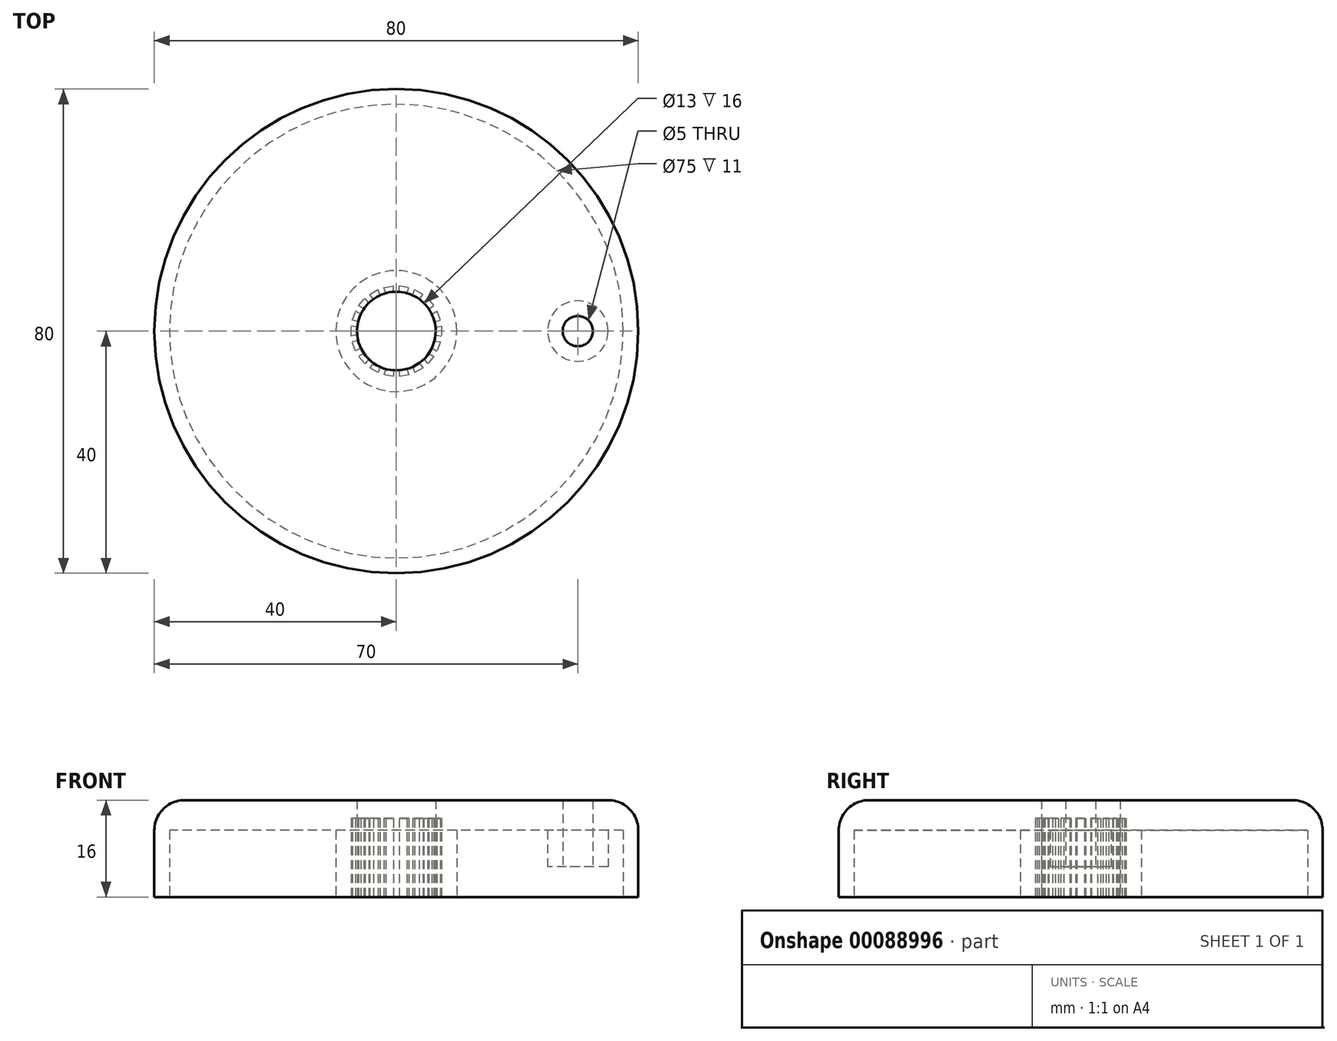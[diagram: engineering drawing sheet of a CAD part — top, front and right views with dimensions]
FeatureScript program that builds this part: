
annotation { "Feature Type Name" : "Feature", "Feature Type Description" : "" }
export const myFeature = defineFeature(function(context is Context, id is Id, definition is map)
    precondition{}
    {
        {
            var Q0;
            Q0=qCreatedBy(makeId("Top.planeOp"),FACE);
            var sketch = newSketch(context, id + "F0", { "sketchPlane" : qUnion([Q0])});
            skCircle(sketch, "E0", {"center": v(0, 0) * mm, "radius": 7.5 * mm, "construction": true});
            skLineSegment(sketch, "E1", {"start": v(0, 0) * mm, "end": v(0, 7.5) * mm, "construction": true});
            skLineSegment(sketch, "E2", {"start": v(0.5, 6.48) * mm, "end": v(0.5, 7.48) * mm});
            skLineSegment(sketch, "E3.MirrorCS", {"start": v(-0.5, 6.48) * mm, "end": v(-0.5, 7.48) * mm});
            skCircle(sketch, "E4.0", {"center": v(0, 0) * mm, "radius": 6.5 * mm, "construction": true});
            skLineSegment(sketch, "E5", {"start": v(-0.5, 6.48) * mm, "end": v(0.5, 6.48) * mm});
            skPoint(sketch, "E6.orphan", {"position": v(-0.5, 5.89) * mm});
            skPoint(sketch, "E7.orphan", {"position": v(0.5, 5.89) * mm});
            skPoint(sketch, "E8.orphan", {"position": v(0.5, 8.94) * mm});
            skPoint(sketch, "E9.orphan", {"position": v(-0.5, 8.94) * mm});
            skLineSegment(sketch, "E10.1.0", {"start": v(1.75, 6.26) * mm, "end": v(2.09, 7.2) * mm});
            skLineSegment(sketch, "E10.1.1", {"start": v(1.75, 6.26) * mm, "end": v(2.69, 5.92) * mm});
            skLineSegment(sketch, "E10.1.2", {"start": v(2.69, 5.92) * mm, "end": v(3.03, 6.86) * mm});
            skLineSegment(sketch, "E10.2.0", {"start": v(3.78, 5.29) * mm, "end": v(4.43, 6.05) * mm});
            skLineSegment(sketch, "E10.2.1", {"start": v(3.78, 5.29) * mm, "end": v(4.55, 4.64) * mm});
            skLineSegment(sketch, "E10.2.2", {"start": v(4.55, 4.64) * mm, "end": v(5.2, 5.41) * mm});
            skLineSegment(sketch, "E10.3.0", {"start": v(5.36, 3.67) * mm, "end": v(6.23, 4.17) * mm});
            skLineSegment(sketch, "E10.3.1", {"start": v(5.36, 3.67) * mm, "end": v(5.86, 2.8) * mm});
            skLineSegment(sketch, "E10.3.2", {"start": v(5.86, 2.8) * mm, "end": v(6.73, 3.3) * mm});
            skLineSegment(sketch, "E10.4.0", {"start": v(6.3, 1.62) * mm, "end": v(7.28, 1.8) * mm});
            skLineSegment(sketch, "E10.4.1", {"start": v(6.3, 1.62) * mm, "end": v(6.47, 0.63) * mm});
            skLineSegment(sketch, "E10.4.2", {"start": v(6.47, 0.63) * mm, "end": v(7.46, 0.8) * mm});
            skLineSegment(sketch, "E10.5.0", {"start": v(6.47, -0.63) * mm, "end": v(7.46, -0.8) * mm});
            skLineSegment(sketch, "E10.5.1", {"start": v(6.47, -0.63) * mm, "end": v(6.3, -1.62) * mm});
            skLineSegment(sketch, "E10.5.2", {"start": v(6.3, -1.62) * mm, "end": v(7.28, -1.8) * mm});
            skLineSegment(sketch, "E10.6.0", {"start": v(5.86, -2.8) * mm, "end": v(6.73, -3.3) * mm});
            skLineSegment(sketch, "E10.6.1", {"start": v(5.86, -2.8) * mm, "end": v(5.36, -3.67) * mm});
            skLineSegment(sketch, "E10.6.2", {"start": v(5.36, -3.67) * mm, "end": v(6.23, -4.17) * mm});
            skLineSegment(sketch, "E10.7.0", {"start": v(4.55, -4.64) * mm, "end": v(5.2, -5.41) * mm});
            skLineSegment(sketch, "E10.7.1", {"start": v(4.55, -4.64) * mm, "end": v(3.78, -5.29) * mm});
            skLineSegment(sketch, "E10.7.2", {"start": v(3.78, -5.29) * mm, "end": v(4.43, -6.05) * mm});
            skLineSegment(sketch, "E10.8.0", {"start": v(2.69, -5.92) * mm, "end": v(3.03, -6.86) * mm});
            skLineSegment(sketch, "E10.8.1", {"start": v(2.69, -5.92) * mm, "end": v(1.75, -6.26) * mm});
            skLineSegment(sketch, "E10.8.2", {"start": v(1.75, -6.26) * mm, "end": v(2.09, -7.2) * mm});
            skLineSegment(sketch, "E10.9.0", {"start": v(0.5, -6.48) * mm, "end": v(0.5, -7.48) * mm});
            skLineSegment(sketch, "E10.9.1", {"start": v(0.5, -6.48) * mm, "end": v(-0.5, -6.48) * mm});
            skLineSegment(sketch, "E10.9.2", {"start": v(-0.5, -6.48) * mm, "end": v(-0.5, -7.48) * mm});
            skLineSegment(sketch, "E10.10.0", {"start": v(-1.75, -6.26) * mm, "end": v(-2.09, -7.2) * mm});
            skLineSegment(sketch, "E10.10.1", {"start": v(-1.75, -6.26) * mm, "end": v(-2.69, -5.92) * mm});
            skLineSegment(sketch, "E10.10.2", {"start": v(-2.69, -5.92) * mm, "end": v(-3.03, -6.86) * mm});
            skLineSegment(sketch, "E10.11.0", {"start": v(-3.78, -5.29) * mm, "end": v(-4.43, -6.05) * mm});
            skLineSegment(sketch, "E10.11.1", {"start": v(-3.78, -5.29) * mm, "end": v(-4.55, -4.64) * mm});
            skLineSegment(sketch, "E10.11.2", {"start": v(-4.55, -4.64) * mm, "end": v(-5.2, -5.41) * mm});
            skLineSegment(sketch, "E10.12.0", {"start": v(-5.36, -3.67) * mm, "end": v(-6.23, -4.17) * mm});
            skLineSegment(sketch, "E10.12.1", {"start": v(-5.36, -3.67) * mm, "end": v(-5.86, -2.8) * mm});
            skLineSegment(sketch, "E10.12.2", {"start": v(-5.86, -2.8) * mm, "end": v(-6.73, -3.3) * mm});
            skLineSegment(sketch, "E10.13.0", {"start": v(-6.3, -1.62) * mm, "end": v(-7.28, -1.8) * mm});
            skLineSegment(sketch, "E10.13.1", {"start": v(-6.3, -1.62) * mm, "end": v(-6.47, -0.63) * mm});
            skLineSegment(sketch, "E10.13.2", {"start": v(-6.47, -0.63) * mm, "end": v(-7.46, -0.8) * mm});
            skLineSegment(sketch, "E10.14.0", {"start": v(-6.47, 0.63) * mm, "end": v(-7.46, 0.8) * mm});
            skLineSegment(sketch, "E10.14.1", {"start": v(-6.47, 0.63) * mm, "end": v(-6.3, 1.62) * mm});
            skLineSegment(sketch, "E10.14.2", {"start": v(-6.3, 1.62) * mm, "end": v(-7.28, 1.8) * mm});
            skLineSegment(sketch, "E10.15.0", {"start": v(-5.86, 2.8) * mm, "end": v(-6.73, 3.3) * mm});
            skLineSegment(sketch, "E10.15.1", {"start": v(-5.86, 2.8) * mm, "end": v(-5.36, 3.67) * mm});
            skLineSegment(sketch, "E10.15.2", {"start": v(-5.36, 3.67) * mm, "end": v(-6.23, 4.17) * mm});
            skLineSegment(sketch, "E10.16.0", {"start": v(-4.55, 4.64) * mm, "end": v(-5.2, 5.41) * mm});
            skLineSegment(sketch, "E10.16.1", {"start": v(-4.55, 4.64) * mm, "end": v(-3.78, 5.29) * mm});
            skLineSegment(sketch, "E10.16.2", {"start": v(-3.78, 5.29) * mm, "end": v(-4.43, 6.05) * mm});
            skLineSegment(sketch, "E10.17.0", {"start": v(-2.69, 5.92) * mm, "end": v(-3.03, 6.86) * mm});
            skLineSegment(sketch, "E10.17.1", {"start": v(-2.69, 5.92) * mm, "end": v(-1.75, 6.26) * mm});
            skLineSegment(sketch, "E10.17.2", {"start": v(-1.75, 6.26) * mm, "end": v(-2.09, 7.2) * mm});
            skLineSegment(sketch, "E10.anchor1", {"start": v(0, 0) * mm, "end": v(-0.5, 6.48) * mm, "construction": true});
            skLineSegment(sketch, "E10.anchor2", {"start": v(0, 0) * mm, "end": v(-2.69, 5.92) * mm, "construction": true});
            skLineSegment(sketch, "E11", {"start": v(-4.43, 6.05) * mm, "end": v(-3.03, 6.86) * mm});
            skLineSegment(sketch, "E12", {"start": v(-2.09, 7.2) * mm, "end": v(-0.5, 7.48) * mm});
            skLineSegment(sketch, "E13", {"start": v(0.5, 7.48) * mm, "end": v(2.09, 7.2) * mm});
            skLineSegment(sketch, "E14", {"start": v(3.03, 6.86) * mm, "end": v(4.43, 6.05) * mm});
            skLineSegment(sketch, "E15", {"start": v(5.2, 5.41) * mm, "end": v(6.23, 4.17) * mm});
            skLineSegment(sketch, "E16", {"start": v(6.73, 3.3) * mm, "end": v(7.28, 1.8) * mm});
            skLineSegment(sketch, "E17", {"start": v(7.46, 0.8) * mm, "end": v(7.46, -0.8) * mm});
            skLineSegment(sketch, "E18", {"start": v(7.28, -1.8) * mm, "end": v(6.73, -3.3) * mm});
            skLineSegment(sketch, "E19", {"start": v(6.23, -4.17) * mm, "end": v(5.2, -5.41) * mm});
            skLineSegment(sketch, "E20", {"start": v(4.43, -6.05) * mm, "end": v(3.03, -6.86) * mm});
            skLineSegment(sketch, "E21", {"start": v(2.09, -7.2) * mm, "end": v(0.5, -7.48) * mm});
            skLineSegment(sketch, "E22", {"start": v(-0.5, -7.48) * mm, "end": v(-2.09, -7.2) * mm});
            skLineSegment(sketch, "E23", {"start": v(-3.03, -6.86) * mm, "end": v(-4.43, -6.05) * mm});
            skLineSegment(sketch, "E24", {"start": v(-5.2, -5.41) * mm, "end": v(-6.23, -4.17) * mm});
            skLineSegment(sketch, "E25", {"start": v(-6.73, -3.3) * mm, "end": v(-7.28, -1.8) * mm});
            skLineSegment(sketch, "E26", {"start": v(-7.46, -0.8) * mm, "end": v(-7.46, 0.8) * mm});
            skLineSegment(sketch, "E27", {"start": v(-7.28, 1.8) * mm, "end": v(-6.73, 3.3) * mm});
            skLineSegment(sketch, "E28", {"start": v(-6.23, 4.17) * mm, "end": v(-5.2, 5.41) * mm});
            skSolve(sketch);
        }
        {
            var Q0;
            Q0=qCreatedBy(makeId("Top.planeOp"),FACE);
            var sketch = newSketch(context, id + "F1", { "sketchPlane" : qUnion([Q0])});
            skCircle(sketch, "E29", {"center": v(0, 0) * mm, "radius": 40 * mm});
            skSolve(sketch);
        }
        {
            var Q0;
            Q0=qSketchRegion(id+"F1",true);
            extrude(context, id + "F2", {"entities" : qUnion([Q0]), "depth" : 16 * mm});
        }
        {
            var Q0;
            Q0=makeQuery(id+"F0.imprint","IMPRINT",FACE,{"disambiguationData":[TD([[makeQuery(id+"F0.imprint","IMPRINT",EDGE,{"derivedFrom":sQuery(id+"F0.wireOp",EDGE,"E2")}),-1.0]])]});
            extrude(context, id + "F3", {"entities" : qUnion([Q0]), "operationType" : NewBodyOperationType.REMOVE, "depth" : 13 * mm});
        }
        {
            var Q0;
            Q0=qCreatedBy(makeId("Top.planeOp"),FACE);
            var sketch = newSketch(context, id + "F4", { "sketchPlane" : qUnion([Q0])});
            skCircle(sketch, "E30", {"center": v(0, 0) * mm, "radius": 6.5 * mm});
            skSolve(sketch);
        }
        {
            var Q0;
            Q0=makeQuery(id+"F4.imprint","IMPRINT",FACE,{"disambiguationData":[TD([[makeQuery(id+"F4.imprint","IMPRINT",EDGE,{"derivedFrom":sQuery(id+"F4.wireOp",EDGE,"E30")}),1.0]])]});
            extrude(context, id + "F5", {"entities" : qUnion([Q0]), "operationType" : NewBodyOperationType.REMOVE, "endBound" : BoundingType.THROUGH_ALL, "depth" : 25 * mm});
        }
        {
            var Q0;
            Q0=qCreatedBy(makeId("Top.planeOp"),FACE);
            var sketch = newSketch(context, id + "F6", { "sketchPlane" : qUnion([Q0])});
            skCircle(sketch, "E31", {"center": v(30, 0) * mm, "radius": 2.5 * mm});
            skSolve(sketch);
        }
        {
            var Q0;
            Q0=makeQuery(id+"F6.imprint","IMPRINT",FACE,{"disambiguationData":[TD([[makeQuery(id+"F6.imprint","IMPRINT",EDGE,{"derivedFrom":sQuery(id+"F6.wireOp",EDGE,"E31")}),1.0]])]});
            extrude(context, id + "F7", {"entities" : qUnion([Q0]), "operationType" : NewBodyOperationType.REMOVE, "endBound" : BoundingType.THROUGH_ALL, "depth" : 25 * mm});
        }
        {
            var Q0;
            Q0=makeQuery(id+"F2.opExtrude","CAP_EDGE",EDGE,{"disambiguationData":[OSD([sQuery(id+"F1.wireOp",EDGE,"E29")])],"isStart":false});
            fillet(context, id + "F8", {"entities" : qUnion([Q0]), "radius" : 5 * mm, "tangentPropagation" : true, "allowEdgeOverflow" : false});
        }
        {
            var Q0;
            Q0=qCreatedBy(makeId("Top.planeOp"),FACE);
            var sketch = newSketch(context, id + "F9", { "sketchPlane" : qUnion([Q0])});
            skCircle(sketch, "E32.0", {"center": v(0, 0) * mm, "radius": 37.5 * mm});
            skCircle(sketch, "E33.0", {"center": v(30, 0) * mm, "radius": 5 * mm});
            skCircle(sketch, "E34", {"center": v(0, 0) * mm, "radius": 10 * mm});
            skSolve(sketch);
        }
        {
            var Q0;
            Q0=makeQuery(id+"F9.imprint","IMPRINT",FACE,{"disambiguationData":[TD([[makeQuery(id+"F9.imprint","IMPRINT",EDGE,{"derivedFrom":sQuery(id+"F9.wireOp",EDGE,"E32.0")}),1.0]])]});
            extrude(context, id + "F10", {"entities" : qUnion([Q0]), "operationType" : NewBodyOperationType.REMOVE, "depth" : 11 * mm});
        }
        {
            var Q0;
            Q0=makeQuery(id+"F10.boolean.opBoolean","SPLIT",FACE,{"disambiguationData":[TD([makeQuery(id+"F7.boolean.opBoolean","COPY",FACE,{"derivedFrom":makeQuery(id+"F7.opExtrude","SWEPT_FACE",FACE,{"disambiguationData":[OSD([sQuery(id+"F6.wireOp",EDGE,"E31")])]})})])],"derivedFrom":makeQuery(id+"F2.opExtrude","CAP_FACE",FACE,{"disambiguationData":[OSD([sQuery(id+"F1.wireOp",EDGE,"E29")])],"isStart":true})});
            extrude(context, id + "F11", {"entities" : qUnion([Q0]), "operationType" : NewBodyOperationType.REMOVE, "oppositeDirection" : true, "depth" : 5 * mm});
        }
    });
